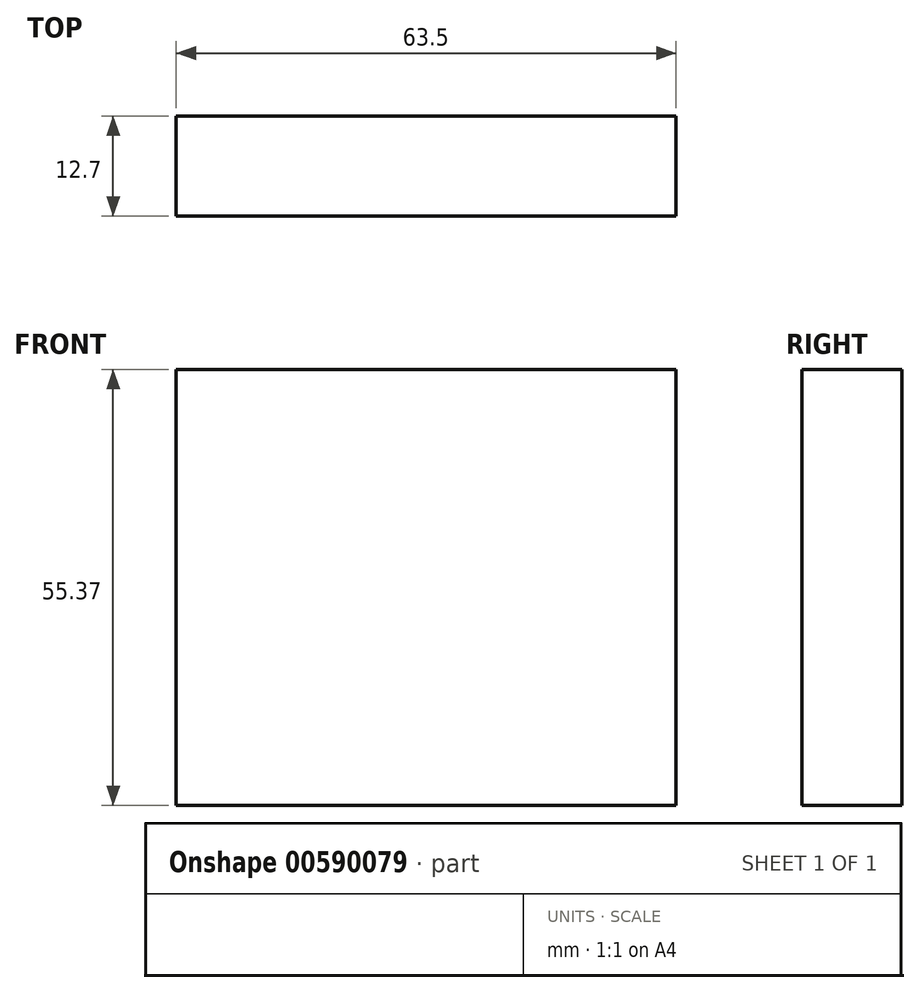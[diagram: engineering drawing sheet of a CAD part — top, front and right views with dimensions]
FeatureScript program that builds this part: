
annotation { "Feature Type Name" : "Feature", "Feature Type Description" : "" }
export const myFeature = defineFeature(function(context is Context, id is Id, definition is map)
    precondition{}
    {
        {
            var Q0;
            Q0=qCreatedBy(makeId("Front.planeOp"),FACE);
            var sketch = newSketch(context, id + "F0", { "sketchPlane" : qUnion([Q0])});
            skLineSegment(sketch, "E0.bottom", {"start": v(-54.4, 58.16) * mm, "end": v(9.1, 58.16) * mm});
            skLineSegment(sketch, "E0.top", {"start": v(-54.4, 2.79) * mm, "end": v(9.1, 2.79) * mm});
            skLineSegment(sketch, "E0.left", {"start": v(-54.4, 58.16) * mm, "end": v(-54.4, 2.79) * mm});
            skLineSegment(sketch, "E0.right", {"start": v(9.1, 58.16) * mm, "end": v(9.1, 2.79) * mm});
            skSolve(sketch);
        }
        {
            var Q0;
            Q0 = qSketchRegion(id + "F0", true);
            extrude(context, id + "F1", {"entities" : qUnion([Q0]), "depth" : 12.7 * mm, "offsetDistance" : 25.4 * mm});
        }
    });
